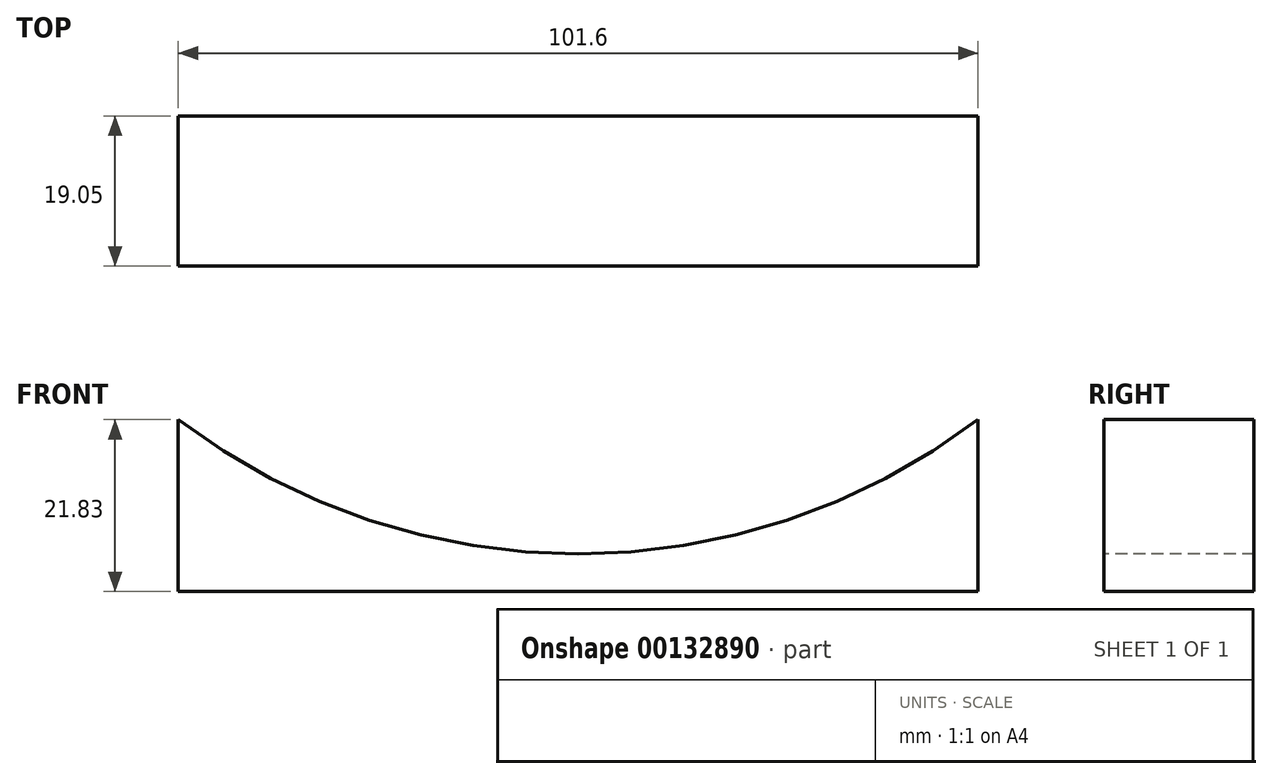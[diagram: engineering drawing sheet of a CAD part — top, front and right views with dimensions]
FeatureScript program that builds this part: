
annotation { "Feature Type Name" : "Feature", "Feature Type Description" : "" }
export const myFeature = defineFeature(function(context is Context, id is Id, definition is map)
    precondition{}
    {
        {
            var Q0;
            Q0=qCreatedBy(makeId("Front.planeOp"),FACE);
            var sketch = newSketch(context, id + "F0", { "sketchPlane" : qUnion([Q0])});
            skLineSegment(sketch, "E0.bottom", {"start": v(54.34, 12.7) * mm, "end": v(-47.26, 12.7) * mm});
            skLineSegment(sketch, "E0.top", {"start": v(54.34, -12.7) * mm, "end": v(-47.26, -12.7) * mm});
            skLineSegment(sketch, "E0.left", {"start": v(54.34, 12.7) * mm, "end": v(54.34, -12.7) * mm});
            skLineSegment(sketch, "E0.right", {"start": v(-47.26, 12.7) * mm, "end": v(-47.26, -12.7) * mm});
            skPoint(sketch, "E0.middle", {"position": v(3.54, 0) * mm});
            skSolve(sketch);
        }
        {
            var Q0;
            Q0=makeQuery(id+"F0.imprint","IMPRINT",FACE,{"disambiguationData":[TD([[makeQuery(id+"F0.imprint","IMPRINT",EDGE,{"derivedFrom":sQuery(id+"F0.wireOp",EDGE,"E0.bottom")}),1.0]])]});
            extrude(context, id + "F1", {"entities" : qUnion([Q0]), "depth" : 19.05 * mm});
        }
        {
            var Q0;
            Q0=makeQuery(id+"F1.opExtrude","CAP_FACE",FACE,{"disambiguationData":[OSD([sQuery(id+"F0.wireOp",EDGE,"E0.bottom"),sQuery(id+"F0.wireOp",EDGE,"E0.top"),sQuery(id+"F0.wireOp",EDGE,"E0.left"),sQuery(id+"F0.wireOp",EDGE,"E0.right")])],"isStart":false});
            var sketch = newSketch(context, id + "F2", { "sketchPlane" : qUnion([Q0])});
            skCircle(sketch, "E1", {"center": v(3.54, 76.2) * mm, "radius": 84.14 * mm});
            skSolve(sketch);
        }
        {
            var Q0;
            {var subQ5=makeQuery(id+"F1.opExtrude","CAP_EDGE",EDGE,{"disambiguationData":[OSD([sQuery(id+"F0.wireOp",EDGE,"E0.bottom")])],"isStart":false});Q0=makeQuery(id+"F2.imprint","IMPRINT",FACE,{"disambiguationData":[TD([[makeQuery(id+"F2.imprint","IMPRINT",EDGE,{"derivedFrom":subQ5}),-1.0]])]});}
            var Q1;
            {var subQ5=makeQuery(id+"F1.opExtrude","CAP_EDGE",EDGE,{"disambiguationData":[OSD([sQuery(id+"F0.wireOp",EDGE,"E0.bottom")])],"isStart":false});Q1=makeQuery(id+"F2.imprint","IMPRINT",FACE,{"disambiguationData":[TD([[makeQuery(id+"F2.imprint","IMPRINT",EDGE,{"derivedFrom":subQ5}),1.0]])]});}
            extrude(context, id + "F3", {"entities" : qUnion([Q0, Q1]), "operationType" : NewBodyOperationType.REMOVE, "endBound" : BoundingType.THROUGH_ALL, "oppositeDirection" : true, "depth" : 25.4 * mm});
        }
    });
